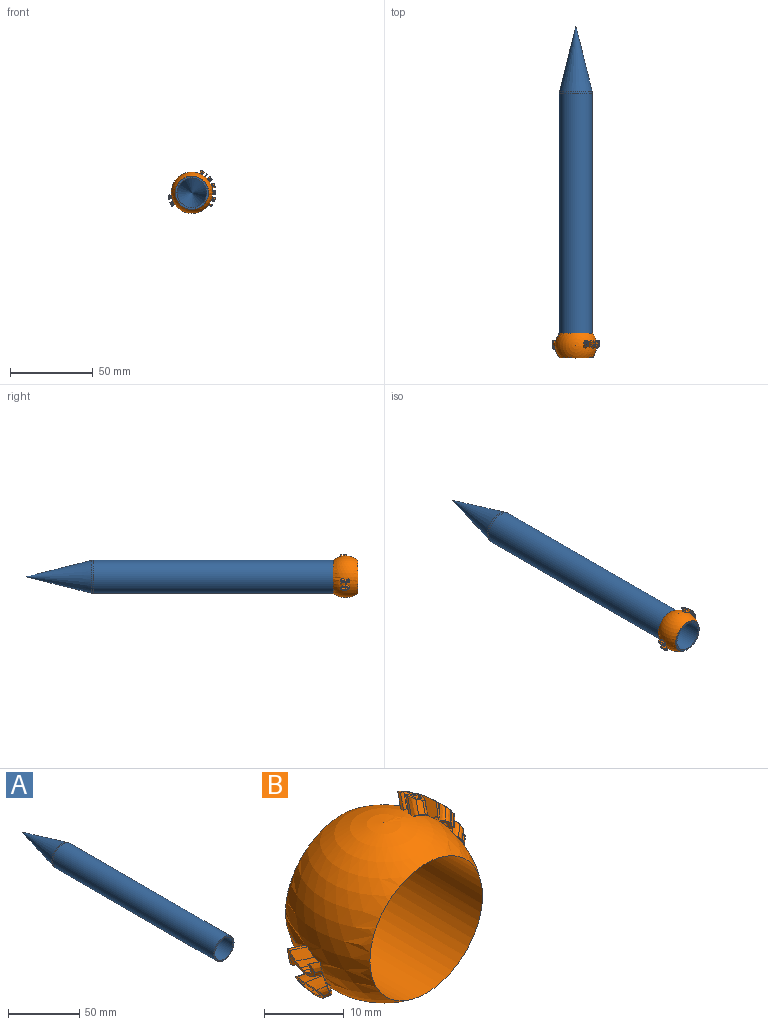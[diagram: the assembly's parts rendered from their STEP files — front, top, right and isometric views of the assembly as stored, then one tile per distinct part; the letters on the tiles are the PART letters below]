
ASSEMBLY  parts=2 mates=1
PART A: 8 faces, bbox 21.6x200x21.6 mm
  f0: cylinder r=9mm len=160mm, axis (0,1,0), area 9047.8mm2, adj f2,f4
  f1: cylinder r=10mm len=159.38mm, axis (0,1,0), area 10014.4mm2, adj f2,f5
  f2: plane 20x20mm, normal (0,-1,0), area 59.7mm2, adj f0,f1
  f3: cone r=10mm half-angle=14deg, axis (0,-1,0), area 1256.9mm2, adj f5
  f4: plane 18x18mm, normal (0,-1,0), area 2.7mm2, adj f0,f6
  f5: torus R=5mm, axis (0,-1,0), area 76.6mm2, adj f1,f3
  f6: torus R=5mm, axis (0,-1,0), area 20.3mm2, adj f4,f7
  f7: cone r=9.03mm half-angle=14deg, axis (0,-1,0), area 1021.5mm2, adj f6
PART B: 170 faces, bbox 29.7x25.3x26.6 mm
  f0: plane 0.93x0.82mm, normal (0.51,-0.8,-0.32), area 0.5mm2, adj f1,f2,f10,f11
  f1: plane 5.55x2.03mm, normal (0.53,0,0.85), area 8.2mm2, adj f0,f9,f10,f11,f63
  f2: plane 5.6x2.04mm, normal (-0.53,0,-0.85), area 8.2mm2, adj f0,f3,f10,f11,f63
  f3: extruded ~1.96x1.84mm, area 1.1mm2, adj f2,f4,f11,f63
  f4: extruded ~1.82x1.48mm, area 1mm2, adj f3,f5,f11,f63
  f5: extruded ~1.71x1.39mm, area 0.9mm2, adj f4,f6,f11,f63
  f6: plane 1.73x1.56mm, normal (-0.53,0,-0.85), area 0.9mm2, adj f5,f7,f11,f63
  f7: extruded ~1.68x1.39mm, area 0.9mm2, adj f6,f8,f11,f63
  f8: extruded ~2.07x1.58mm, area 1.8mm2, adj f7,f9,f11,f63
  f9: extruded ~2.29x2.19mm, area 1.9mm2, adj f1,f8,f11,f63
  f10: plane 1.5x1.2mm, normal (-0.68,-0.6,0.43), area 0.9mm2, adj f0,f1,f2,f63
  f11: sphere r=14.5mm, area 2.9mm2, adj f0,f1,f2,f3,f4,f5,f6,f7
  f12: extruded ~1.68x1.53mm, area 1.9mm2, adj f13,f22,f31,f32
  f13: extruded ~2.13x1.6mm, area 2.1mm2, adj f12,f23,f31,f32
  f14: extruded ~2.04x1.55mm, area 1.4mm2, adj f15,f28,f31,f32
  f15: extruded ~1.79x1.54mm, area 1.3mm2, adj f14,f29,f31,f32
  f16: plane 1.82x1.81mm, normal (0.29,0,0.96), area 0.9mm2, adj f17,f30,f32,f63
  f17: extruded ~2.26x1.63mm, area 2.2mm2, adj f16,f18,f32,f63
  f18: extruded ~1.96x1.69mm, area 1.8mm2, adj f17,f19,f32,f63
  f19: extruded ~2.57x2.35mm, area 2mm2, adj f18,f20,f32,f63
  f20: plane 2.55x2.45mm, normal (-0.57,0.8,0.18), area 4.9mm2, adj f19,f21,f32,f63
  f21: plane 1.88x1.81mm, normal (0.29,0,0.96), area 0.7mm2, adj f20,f22,f32,f63
  f22: extruded ~2.53x2.39mm, area 2.5mm2, adj f12,f21,f31,f32,f63
  f23: extruded ~2.93x2.61mm, area 2.9mm2, adj f13,f24,f31,f32,f63
  f24: extruded ~2.87x2.72mm, area 2.8mm2, adj f23,f25,f32,f63
  f25: extruded ~2.03x1.82mm, area 2.6mm2, adj f24,f26,f32,f63
  f26: extruded ~1.92x1.4mm, area 1.1mm2, adj f25,f30,f32,f63
  f27: plane 2.34x2.05mm, normal (0.57,-0.8,-0.18), area 3.8mm2, adj f28,f29,f32,f63
  f28: extruded ~2.5x2.13mm, area 1.7mm2, adj f14,f27,f31,f32,f63
  f29: extruded ~2.38x2.13mm, area 1.7mm2, adj f15,f27,f31,f32,f63
  f30: extruded ~2.02x1.53mm, area 1.1mm2, adj f16,f26,f32,f63
  f31: plane 2.35x1.1mm, normal (-0.77,-0.6,0.23), area 1.1mm2, adj f12,f13,f14,f15,f22,f23,f28,f29
  f32: sphere r=14.5mm, area 3.8mm2, adj f12,f13,f14,f15,f16,f17,f18,f19
  f33: plane 2.04x0.81mm, normal (-0.8,-0.6,-0.01), area 0.9mm2, adj f34,f45,f46,f47,f48,f49,f50,f51
  f34: plane 3.79x2.1mm, normal (-0.01,0,1), area 4.8mm2, adj f33,f35,f52,f61,f63
  f35: plane 1.82x1.37mm, normal (-0.6,0.8,-0.01), area 0.7mm2, adj f34,f36,f61,f63
  f36: plane 1.89x1.83mm, normal (-0.11,0.16,-0.98), area 1mm2, adj f35,f37,f61,f63
  f37: plane 1.83x1.37mm, normal (-0.6,0.8,-0.01), area 0mm2, adj f36,f38,f61,f63
  f38: extruded ~2.21x1.79mm, area 1.3mm2, adj f37,f39,f61,f63
  f39: extruded ~1.88x1.45mm, area 1.3mm2, adj f38,f40,f61,f63
  f40: extruded ~2.07x1.62mm, area 1.7mm2, adj f39,f41,f61,f63
  f41: extruded ~2.54x2.13mm, area 1.6mm2, adj f40,f42,f61,f63
  f42: extruded ~2.9x2.52mm, area 4.6mm2, adj f41,f43,f61,f63
  f43: plane 1.99x1.51mm, normal (0.6,-0.8,-0.03), area 1.2mm2, adj f42,f44,f61,f63
  f44: plane 2x1.72mm, normal (0.01,0,-1), area 0.5mm2, adj f43,f45,f61,f63
  f45: extruded ~2.37x1.95mm, area 1.3mm2, adj f33,f44,f46,f61,f63
  f46: extruded ~1.88x1.47mm, area 1.1mm2, adj f33,f45,f47,f61
  f47: extruded ~1.93x1.53mm, area 1.9mm2, adj f33,f46,f48,f61
  f48: plane 1.8x1.63mm, normal (-0.21,0.3,-0.93), area 0.8mm2, adj f33,f47,f49,f61
  f49: extruded ~1.7x1.34mm, area 1mm2, adj f33,f48,f50,f61
  f50: extruded ~1.53x1.18mm, area 1mm2, adj f33,f49,f51,f61
  f51: extruded ~1.73x1.37mm, area 1.6mm2, adj f33,f50,f52,f61
  f52: extruded ~2.45x2.1mm, area 1.8mm2, adj f33,f34,f51,f61
  f53: extruded ~2.38x1.94mm, area 1.3mm2, adj f54,f60,f61,f62
  f54: extruded ~2.09x1.63mm, area 1.9mm2, adj f53,f55,f61,f62
  f55: plane 1.95x1.48mm, normal (-0.6,0.8,0.03), area 1.1mm2, adj f54,f56,f61,f62
  f56: plane 1.94x1.76mm, normal (0.01,0,-1), area 0.6mm2, adj f55,f57,f61,f62
  f57: extruded ~2.57x2.15mm, area 1.6mm2, adj f56,f58,f61,f62
  f58: extruded ~2.06x1.63mm, area 1.6mm2, adj f57,f59,f61,f62
  f59: extruded ~1.97x1.52mm, area 1mm2, adj f58,f60,f61,f62
  f60: extruded ~2.25x1.81mm, area 0.9mm2, adj f53,f59,f61,f62
  f61: sphere r=14.5mm, area 4mm2, adj f34,f35,f36,f37,f38,f39,f40,f41
  f62: sphere r=12.5mm, area 1.5mm2, adj f53,f54,f55,f56,f57,f58,f59,f60
  f63: sphere r=12.5mm, area 1155.4mm2, adj f1,f2,f3,f4,f5,f6,f7,f8
  f64: plane 1.44x1.29mm, normal (0.38,-0.8,0.47), area 0.8mm2, adj f65,f67,f68,f69
  f65: plane 4.81x1.89mm, normal (0.77,0,-0.63), area 6.8mm2, adj f63,f64,f66,f68,f69
  f66: plane 1.67x1.48mm, normal (-0.38,0.8,-0.47), area 1mm2, adj f63,f65,f67,f69
  f67: plane 4.82x1.9mm, normal (-0.77,0,0.63), area 6.8mm2, adj f63,f64,f66,f68,f69
  f68: plane 0.71x0.7mm, normal (-0.51,-0.6,-0.62), area 0.4mm2, adj f63,f64,f65,f67
  f69: sphere r=14.5mm, area 1.5mm2, adj f64,f65,f66,f67
  f70: extruded ~1.69x1.62mm, area 1.9mm2, adj f71,f80,f89,f90
  f71: extruded ~2.16x1.6mm, area 2.1mm2, adj f70,f81,f89,f90
  f72: extruded ~2x1.55mm, area 1.4mm2, adj f73,f86,f89,f90
  f73: extruded ~1.75x1.54mm, area 1.3mm2, adj f72,f87,f89,f90
  f74: plane 1.83x1.7mm, normal (-0.9,0,0.45), area 0.9mm2, adj f63,f75,f88,f90
  f75: extruded ~2.28x1.66mm, area 2.2mm2, adj f63,f74,f76,f90
  f76: extruded ~1.93x1.69mm, area 1.8mm2, adj f63,f75,f77,f90
  f77: extruded ~2.36x2.35mm, area 2mm2, adj f63,f76,f78,f90
  f78: plane 2.71x2.62mm, normal (-0.27,0.8,-0.54), area 4.9mm2, adj f63,f77,f79,f90
  f79: plane 1.81x1.77mm, normal (-0.9,0,0.45), area 0.7mm2, adj f63,f78,f80,f90
  f80: extruded ~2.39x2.31mm, area 2.4mm2, adj f63,f70,f79,f89,f90
  f81: extruded ~2.8x2.61mm, area 2.9mm2, adj f63,f71,f82,f89,f90
  f82: extruded ~2.72x2.62mm, area 2.8mm2, adj f63,f81,f83,f90
  f83: extruded ~2.04x1.92mm, area 2.6mm2, adj f63,f82,f84,f90
  f84: extruded ~1.88x1.4mm, area 1.1mm2, adj f63,f83,f88,f90
  f85: plane 2.46x2.26mm, normal (0.27,-0.8,0.54), area 3.8mm2, adj f63,f86,f87,f90
  f86: extruded ~2.38x2.13mm, area 1.7mm2, adj f63,f72,f85,f89,f90
  f87: extruded ~2.19x2.13mm, area 1.7mm2, adj f63,f73,f85,f89,f90
  f88: extruded ~1.97x1.53mm, area 1.1mm2, adj f63,f74,f84,f90
  f89: plane 2.2x1.36mm, normal (-0.36,-0.6,-0.72), area 1.1mm2, adj f63,f70,f71,f72,f73,f80,f81,f86
  f90: sphere r=14.5mm, area 3.9mm2, adj f70,f71,f72,f73,f74,f75,f76,f77
  f91: extruded ~2.27x2.02mm, area 1.6mm2, adj f92,f104,f111,f112
  f92: extruded ~1.94x1.7mm, area 1.3mm2, adj f91,f93,f111,f112
  f93: extruded ~1.27x1mm, area 1mm2, adj f92,f94,f111,f112
  f94: extruded ~1.41x1.14mm, area 1.5mm2, adj f93,f95,f111,f112
  f95: plane 1.25x1.2mm, normal (0.21,0.49,0.85), area 0.6mm2, adj f94,f96,f111,f112
  f96: extruded ~1.33x1.19mm, area 0.8mm2, adj f95,f97,f111,f112
  f97: extruded ~1.12x0.89mm, area 0.6mm2, adj f96,f98,f111,f112
  f98: extruded ~1.36x1.03mm, area 0.8mm2, adj f97,f99,f111,f112
  f99: extruded ~1.8x1.52mm, area 0.9mm2, adj f98,f100,f111,f112
  f100: extruded ~1.95x1.65mm, area 0.9mm2, adj f99,f101,f111,f112
  f101: extruded ~2.14x1.81mm, area 1.1mm2, adj f100,f105,f111,f112
  f102: plane 1.8x1.4mm, normal (0.19,0,-0.98), area 0mm2, adj f63,f103,f110,f112
  f103: plane 2.38x1.91mm, normal (0.55,0.57,-0.6), area 2.8mm2, adj f63,f102,f104,f112
  f104: extruded ~2.76x2.54mm, area 3mm2, adj f63,f91,f103,f111,f112
  f105: extruded ~2.58x2.3mm, area 2.3mm2, adj f63,f101,f106,f111,f112
  f106: plane 2.6x1.92mm, normal (-0.55,-0.57,0.62), area 3.4mm2, adj f63,f105,f107,f112
  f107: plane 1.85x1.79mm, normal (-0.19,0,0.98), area 0.9mm2, adj f63,f106,f108,f112
  f108: plane 2.88x2.25mm, normal (0.59,0.8,0.11), area 5.8mm2, adj f63,f107,f109,f112
  f109: plane 1.86x1.83mm, normal (0.19,0,-0.98), area 0.9mm2, adj f63,f108,f110,f112
  f110: plane 2.32x2.21mm, normal (-0.59,-0.8,-0.11), area 4.6mm2, adj f63,f102,f109,f112
  f111: plane 2.3x1.57mm, normal (0.79,-0.6,0.15), area 1.5mm2, adj f63,f91,f92,f93,f94,f95,f96,f97
  f112: sphere r=14.5mm, area 4.1mm2, adj f91,f92,f93,f94,f95,f96,f97,f98
  f113: extruded ~1.53x1.22mm, area 1.3mm2, adj f114,f118,f129,f130
  f114: extruded ~2.72x2.39mm, area 3.1mm2, adj f113,f119,f129,f130
  f115: extruded ~2.71x2.7mm, area 3.1mm2, adj f118,f122,f129,f130
  f116: extruded ~1.66x1.3mm, area 1.2mm2, adj f117,f123,f129,f130
  f117: extruded ~1.31x1.29mm, area 1.2mm2, adj f116,f128,f129,f130
  f118: extruded ~1.72x1.25mm, area 1.4mm2, adj f113,f115,f129,f130
  f119: extruded ~3.34x3.26mm, area 3.8mm2, adj f63,f114,f120,f129,f130
  f120: extruded ~2.54x1.96mm, area 2.6mm2, adj f63,f119,f121,f130
  f121: extruded ~2.03x2.01mm, area 2.6mm2, adj f63,f120,f122,f130
  f122: extruded ~3.27x3.03mm, area 3.8mm2, adj f63,f115,f121,f129,f130
  f123: extruded ~2.53x2.52mm, area 2.7mm2, adj f63,f116,f124,f129,f130
  f124: extruded ~2.95x2.83mm, area 3.1mm2, adj f63,f123,f125,f130
  f125: extruded ~1.91x1.84mm, area 1.8mm2, adj f63,f124,f126,f130
  f126: extruded ~2.29x1.84mm, area 1.8mm2, adj f63,f125,f127,f130
  f127: extruded ~3.03x2.95mm, area 3.1mm2, adj f63,f126,f128,f130
  f128: extruded ~2.52x2.33mm, area 2.7mm2, adj f63,f117,f127,f129,f130
  f129: plane 2.52x2mm, normal (0.7,-0.6,0.39), area 2mm2, adj f63,f113,f114,f115,f116,f117,f118,f119
  f130: sphere r=14.5mm, area 4.7mm2, adj f113,f114,f115,f116,f117,f118,f119,f120
  f131: extruded ~1.9x1.39mm, area 1.6mm2, adj f132,f139,f148,f149
  f132: extruded ~1.56x1.24mm, area 1.1mm2, adj f131,f133,f148,f149
  f133: extruded ~1.7x1.56mm, area 1.1mm2, adj f132,f134,f148,f149
  f134: plane 1.64x1.29mm, normal (0.57,-0.8,0.19), area 0mm2, adj f133,f135,f148,f149
  f135: plane 1.65x1.62mm, normal (-0.21,-0.14,0.97), area 0.8mm2, adj f134,f136,f148,f149
  f136: plane 1.49x1.11mm, normal (0.57,-0.8,0.19), area 0.7mm2, adj f135,f140,f148,f149
  f137: extruded ~1.83x1.57mm, area 1.6mm2, adj f138,f143,f148,f149
  f138: extruded ~1.96x1.48mm, area 1.2mm2, adj f137,f144,f148,f149
  f139: extruded ~2.48x2.18mm, area 2mm2, adj f63,f131,f147,f148,f149
  f140: plane 4.53x2.01mm, normal (0.32,0,-0.95), area 6.8mm2, adj f63,f136,f141,f148,f149
  f141: plane 1.82x1.37mm, normal (-0.57,0.8,-0.19), area 1mm2, adj f63,f140,f142,f149
  f142: plane 3.21x1.97mm, normal (-0.32,0,0.95), area 3.6mm2, adj f63,f141,f143,f149
  f143: extruded ~2.54x2.36mm, area 2.1mm2, adj f63,f137,f142,f148,f149
  f144: extruded ~2.32x1.98mm, area 1.4mm2, adj f63,f138,f145,f148,f149
  f145: plane 3.65x1.98mm, normal (0.32,0,-0.95), area 4.5mm2, adj f63,f144,f146,f149
  f146: plane 1.88x1.38mm, normal (-0.57,0.8,-0.19), area 1mm2, adj f63,f145,f147,f149
  f147: plane 3.68x1.99mm, normal (-0.32,0,0.95), area 4.5mm2, adj f63,f139,f146,f149
  f148: plane 2.4x1.37mm, normal (-0.76,-0.6,-0.25), area 1.3mm2, adj f63,f131,f132,f133,f134,f135,f136,f137
  f149: sphere r=14.5mm, area 3.7mm2, adj f131,f132,f133,f134,f135,f136,f137,f138
  f150: extruded ~1.87x1.51mm, area 1.6mm2, adj f151,f158,f167,f168
  f151: extruded ~1.49x1.41mm, area 1.1mm2, adj f150,f152,f167,f168
  f152: extruded ~1.56x1.48mm, area 1.1mm2, adj f151,f153,f167,f168
  f153: plane 1.38x1.29mm, normal (0.48,-0.8,0.36), area 0mm2, adj f152,f154,f167,f168
  f154: plane 1.62x1.41mm, normal (-0.51,-0.14,0.85), area 0.8mm2, adj f153,f155,f167,f168
  f155: plane 1.37x1.18mm, normal (0.48,-0.8,0.36), area 0.7mm2, adj f154,f159,f167,f168
  f156: extruded ~1.75x1.74mm, area 1.6mm2, adj f157,f162,f167,f168
  f157: extruded ~1.81x1.48mm, area 1.2mm2, adj f156,f163,f167,f168
  f158: extruded ~2.18x2.17mm, area 2mm2, adj f63,f150,f166,f167,f168
  f159: plane 4.53x1.69mm, normal (0.61,0,-0.79), area 6.8mm2, adj f63,f155,f160,f167,f168
  f160: plane 1.68x1.47mm, normal (-0.48,0.8,-0.36), area 1mm2, adj f63,f159,f161,f168
  f161: plane 3.19x1.64mm, normal (-0.61,0,0.79), area 3.6mm2, adj f63,f160,f162,f168
  f162: extruded ~2.36x2.06mm, area 2.1mm2, adj f63,f156,f161,f167,f168
  f163: extruded ~2x1.98mm, area 1.4mm2, adj f63,f157,f164,f167,f168
  f164: plane 3.65x1.66mm, normal (0.61,0,-0.79), area 4.5mm2, adj f63,f163,f165,f168
  f165: plane 1.73x1.43mm, normal (-0.48,0.8,-0.36), area 1mm2, adj f63,f164,f166,f168
  f166: plane 3.68x1.67mm, normal (-0.61,0,0.79), area 4.5mm2, adj f63,f158,f165,f168
  f167: plane 2.1x1.99mm, normal (-0.64,-0.6,-0.49), area 1.3mm2, adj f63,f150,f151,f152,f153,f154,f155,f156
  f168: sphere r=14.5mm, area 3.8mm2, adj f150,f151,f152,f153,f154,f155,f156,f157
  f169: cylinder r=10mm len=20mm, axis (0,-1,0), area 942.5mm2, adj f63
PLACE A t=(28.65,194.23,37.25)mm
PLACE B t=(28.65,41.73,37.25)mm
MATE fastened A.f0 <-> B.f169  axis (0,1,0) through (28.65,34.23,37.25)mm
